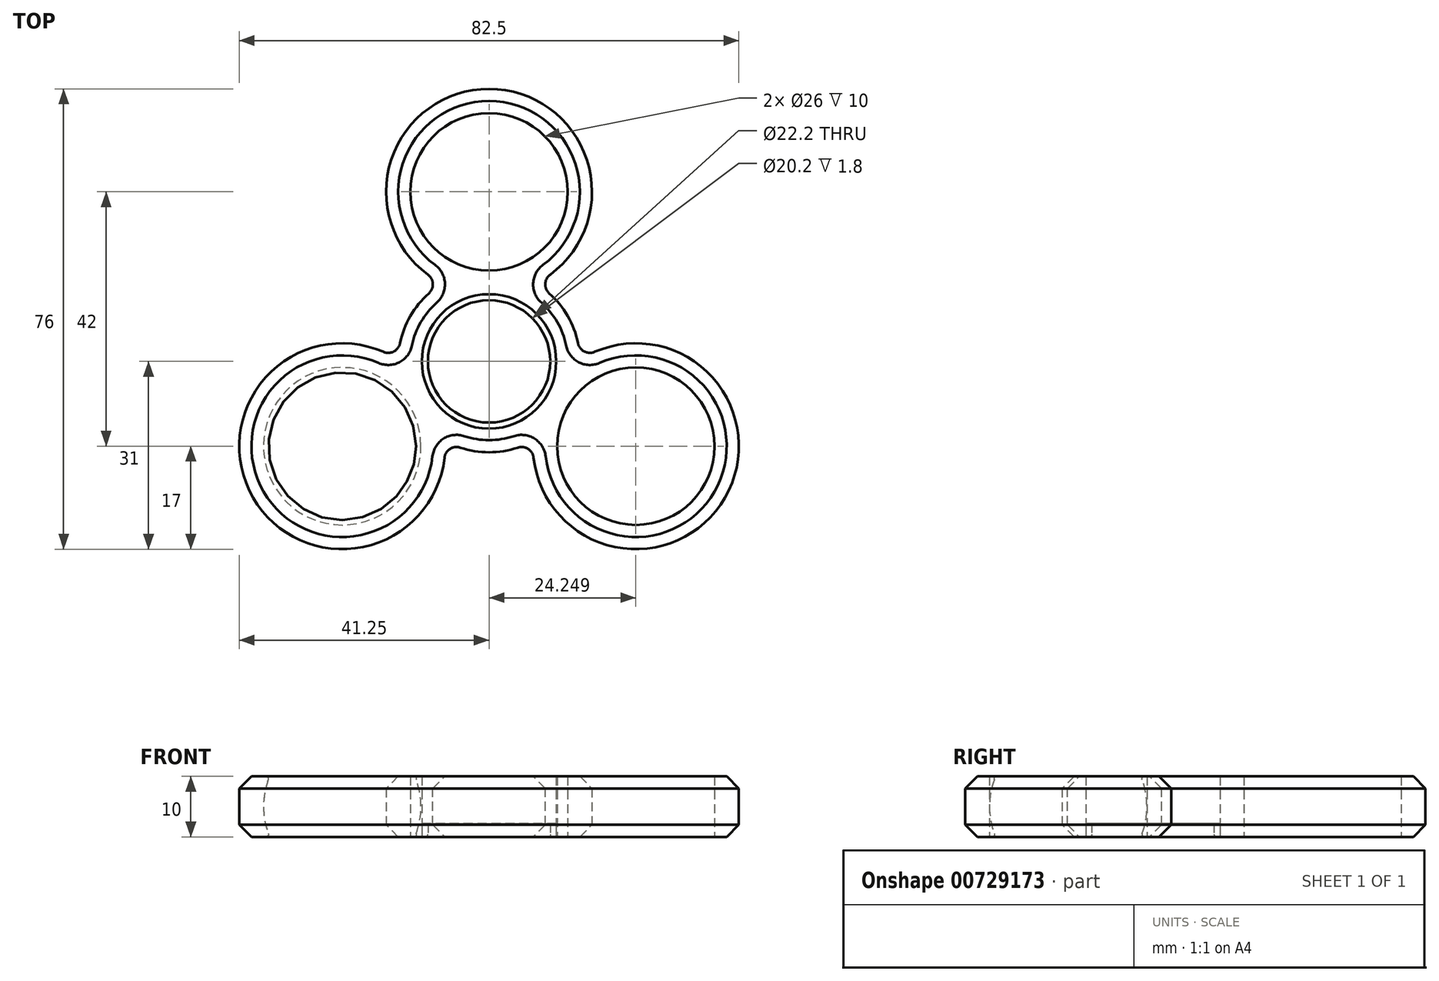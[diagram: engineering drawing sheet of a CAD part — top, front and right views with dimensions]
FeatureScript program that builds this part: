
annotation { "Feature Type Name" : "Feature", "Feature Type Description" : "" }
export const myFeature = defineFeature(function(context is Context, id is Id, definition is map)
    precondition{}
    {
        {
            var Q0;
            Q0=qCreatedBy(makeId("Top.planeOp"),FACE);
            var sketch = newSketch(context, id + "F0", { "sketchPlane" : qUnion([Q0])});
            skLineSegment(sketch, "E0", {"start": v(0, 0) * mm, "end": v(0, 28) * mm, "construction": true});
            skCircle(sketch, "E1", {"center": v(0, 28) * mm, "radius": 13 * mm});
            skArc(sketch, "E2", {"start": v(7.73, 12.86) * mm, "mid": v(0, 45) * mm, "end": v(-7.73, 12.86) * mm});
            skCircle(sketch, "E3", {"center": v(0, 0) * mm, "radius": 11.1 * mm});
            skArc(sketch, "E4", {"start": v(-7.27, -13.12) * mm, "mid": v(0, -15) * mm, "end": v(7.27, -13.12) * mm});
            skArc(sketch, "E5.1.2", {"start": v(-15, 0.26) * mm, "mid": v(-38.97, -22.5) * mm, "end": v(-7.27, -13.12) * mm});
            skCircle(sketch, "E5.1.3", {"center": v(-24.25, -14) * mm, "radius": 13 * mm});
            skArc(sketch, "E5.2.2", {"start": v(7.27, -13.12) * mm, "mid": v(38.97, -22.5) * mm, "end": v(15, 0.26) * mm});
            skCircle(sketch, "E5.2.3", {"center": v(24.25, -14) * mm, "radius": 13 * mm});
            skArc(sketch, "E6.trimOffspring", {"start": v(15, 0.26) * mm, "mid": v(13, 7.5) * mm, "end": v(7.73, 12.86) * mm});
            skArc(sketch, "E7.trimOffspring", {"start": v(-7.73, 12.86) * mm, "mid": v(-13, 7.5) * mm, "end": v(-15, 0.26) * mm});
            skLineSegment(sketch, "E8", {"start": v(0, 0) * mm, "end": v(-24.25, -14) * mm, "construction": true});
            skLineSegment(sketch, "E9", {"start": v(0, 0) * mm, "end": v(24.25, -14) * mm, "construction": true});
            skSolve(sketch);
        }
        {
            var Q0;
            Q0=qSketchRegion(id+"F0",true);
            extrude(context, id + "F1", {"entities" : qUnion([Q0]), "depth" : 10 * mm, "offsetDistance" : 25 * mm});
        }
        {
            var Q0;
            Q0=makeQuery(id+"F1.opExtrude","SWEPT_EDGE",EDGE,{"disambiguationData":[OSD([sQuery(id+"F0.wireOp",EDGE,"E4"),sQuery(id+"F0.wireOp",EDGE,"E5.1.2")])]});
            var Q1;
            Q1=makeQuery(id+"F1.opExtrude","SWEPT_EDGE",EDGE,{"disambiguationData":[OSD([sQuery(id+"F0.wireOp",EDGE,"E4"),sQuery(id+"F0.wireOp",EDGE,"E5.2.2")])]});
            var Q2;
            Q2=makeQuery(id+"F1.opExtrude","SWEPT_EDGE",EDGE,{"disambiguationData":[OSD([sQuery(id+"F0.wireOp",EDGE,"E5.2.2"),sQuery(id+"F0.wireOp",EDGE,"E6.trimOffspring")])]});
            var Q3;
            Q3=makeQuery(id+"F1.opExtrude","SWEPT_EDGE",EDGE,{"disambiguationData":[OSD([sQuery(id+"F0.wireOp",EDGE,"E2"),sQuery(id+"F0.wireOp",EDGE,"E6.trimOffspring")])]});
            var Q4;
            Q4=makeQuery(id+"F1.opExtrude","SWEPT_EDGE",EDGE,{"disambiguationData":[OSD([sQuery(id+"F0.wireOp",EDGE,"E2"),sQuery(id+"F0.wireOp",EDGE,"E7.trimOffspring")])]});
            var Q5;
            Q5=makeQuery(id+"F1.opExtrude","SWEPT_EDGE",EDGE,{"disambiguationData":[OSD([sQuery(id+"F0.wireOp",EDGE,"E5.1.2"),sQuery(id+"F0.wireOp",EDGE,"E7.trimOffspring")])]});
            fillet(context, id + "F2", {"entities" : qUnion([Q0, Q1, Q2, Q3, Q4, Q5]), "radius" : 2 * mm, "tangentPropagation" : true, "allowEdgeOverflow" : false});
        }
        {
            var Q0;
            Q0=makeQuery(id+"F1.opExtrude","CAP_EDGE",EDGE,{"disambiguationData":[OSD([sQuery(id+"F0.wireOp",EDGE,"E5.2.2")])],"isStart":true});
            var Q1;
            Q1=makeQuery(id+"F1.opExtrude","CAP_EDGE",EDGE,{"disambiguationData":[OSD([sQuery(id+"F0.wireOp",EDGE,"E5.2.2")])],"isStart":false});
            chamfer(context, id + "F3", {"entities" : qUnion([Q0, Q1]), "width" : 2 * mm, "tangentPropagation" : true});
        }
        {
            var Q0;
            Q0=qCreatedBy(makeId("Top.planeOp"),FACE);
            var sketch = newSketch(context, id + "F4", { "sketchPlane" : qUnion([Q0])});
            skCircle(sketch, "E10.0", {"center": v(-24.25, -14) * mm, "radius": 13 * mm, "construction": true});
            skLineSegment(sketch, "E11", {"start": v(0, 0) * mm, "end": v(-24.25, -14) * mm, "construction": true});
            skCircle(sketch, "E12.0", {"center": v(0, 28) * mm, "radius": 13 * mm, "construction": true});
            skLineSegment(sketch, "E13", {"start": v(0, 0) * mm, "end": v(0, 28) * mm, "construction": true});
            skCircle(sketch, "E14.0", {"center": v(24.25, -14) * mm, "radius": 13 * mm, "construction": true});
            skLineSegment(sketch, "E15", {"start": v(0, 0) * mm, "end": v(24.25, -14) * mm, "construction": true});
            skSolve(sketch);
        }
        {
            var Q0;
            {var subQ0=sQuery(id+"F0.wireOp",EDGE,"E5.1.2");Q0=makeQuery(id+"F3.opChamfer","BLEND_EDGE",EDGE,{"blendedFrom":[makeQuery(id+"F1.opExtrude","CAP_EDGE",EDGE,{"disambiguationData":[OSD([subQ0])],"isStart":false}),makeQuery(id+"F1.opExtrude","CAP_FACE",FACE,{"disambiguationData":[OSD([sQuery(id+"F0.wireOp",EDGE,"E1"),sQuery(id+"F0.wireOp",EDGE,"E2"),sQuery(id+"F0.wireOp",EDGE,"E3"),sQuery(id+"F0.wireOp",EDGE,"E4"),subQ0,sQuery(id+"F0.wireOp",EDGE,"E5.1.3"),sQuery(id+"F0.wireOp",EDGE,"E5.2.2"),sQuery(id+"F0.wireOp",EDGE,"E5.2.3"),sQuery(id+"F0.wireOp",EDGE,"E6.trimOffspring"),sQuery(id+"F0.wireOp",EDGE,"E7.trimOffspring")])],"isStart":false})],"blendedInto":[makeQuery(id+"F1.opExtrude","CAP_FACE",FACE,{"disambiguationData":[OSD([sQuery(id+"F0.wireOp",EDGE,"E1"),sQuery(id+"F0.wireOp",EDGE,"E2"),sQuery(id+"F0.wireOp",EDGE,"E3"),sQuery(id+"F0.wireOp",EDGE,"E4"),subQ0,sQuery(id+"F0.wireOp",EDGE,"E5.1.3"),sQuery(id+"F0.wireOp",EDGE,"E5.2.2"),sQuery(id+"F0.wireOp",EDGE,"E5.2.3"),sQuery(id+"F0.wireOp",EDGE,"E6.trimOffspring"),sQuery(id+"F0.wireOp",EDGE,"E7.trimOffspring")])],"isStart":false})]});}
            cPoint(context, id + "F5", {"entities" : qUnion([Q0]), "parameter" : 0.5});
        }
        {
            var Q0;
            Q0=sQuery(id+"F4.wireOp",VERTEX,"E11.start");
            var Q1;
            Q1=sQuery(id+"F4.wireOp",VERTEX,"E10.0.center");
            var Q2;
            Q2=qCreatedBy(id+"F5",VERTEX);
            cPlane(context, id + "F6", {"entities" : qUnion([Q0, Q1, Q2]), "cplaneType" : CPlaneType.THREE_POINT, "offset" : 25 * mm, "width" : 150 * mm, "height" : 150 * mm});
        }
        {
            var Q0;
            Q0=qCreatedBy(id+"F6.planeOp",FACE);
            var sketch = newSketch(context, id + "F7", { "sketchPlane" : qUnion([Q0])});
            skLineSegment(sketch, "E16.0", {"start": v(-41, 10) * mm, "end": v(-40, 10) * mm, "construction": true});
            skLineSegment(sketch, "E17.1", {"start": v(-41, 0) * mm, "end": v(-40, 0) * mm, "construction": true});
            skLineSegment(sketch, "E18", {"start": v(-41, 10) * mm, "end": v(-41, 0) * mm});
            skLineSegment(sketch, "E19", {"start": v(-28, 0) * mm, "end": v(-28, 10) * mm, "construction": true});
            skArc(sketch, "E20", {"start": v(-40, 10) * mm, "mid": v(-41, 5) * mm, "end": v(-40, 0) * mm});
            skLineSegment(sketch, "E21", {"start": v(-41, 10) * mm, "end": v(-40, 10) * mm});
            skLineSegment(sketch, "E22", {"start": v(-41, 0) * mm, "end": v(-40, 0) * mm});
            skLineSegment(sketch, "E23.trimOffspring", {"start": v(-28, 10) * mm, "end": v(-15, 10) * mm, "construction": true});
            skLineSegment(sketch, "E24.trimOffspring", {"start": v(-28, 0) * mm, "end": v(-15, 0) * mm, "construction": true});
            skSolve(sketch);
        }
        {
            var Q0;
            Q0=qSketchRegion(id+"F7",true);
            var Q1;
            Q1=sQuery(id+"F7.wireOp",EDGE,"E19");
            revolve(context, id + "F8", {"operationType" : NewBodyOperationType.ADD, "surfaceOperationType" : NewSurfaceOperationType.NEW, "entities" : qUnion([Q0]), "axis" : qUnion([Q1]), "revolveType" : RevolveType.FULL});
        }
        {
            var Q0;
            {var subQ0=sQuery(id+"F7.wireOp",EDGE,"E22");Q0=makeQuery(id+"FEcUt43eDZ80vxZ_1.2.F8.boolean.opBoolean","MERGE",FACE,{"derivedFrom":[makeQuery(id+"Fynh9oEJvHPlE7w_1.2.F8.boolean.opBoolean","MERGE",FACE,{"derivedFrom":[makeQuery(id+"F8.boolean.opBoolean","MERGE",FACE,{"derivedFrom":[makeQuery(id+"F1.opExtrude","CAP_FACE",FACE,{"disambiguationData":[OSD([sQuery(id+"F0.wireOp",EDGE,"E1"),sQuery(id+"F0.wireOp",EDGE,"E2"),sQuery(id+"F0.wireOp",EDGE,"E3"),sQuery(id+"F0.wireOp",EDGE,"E4"),sQuery(id+"F0.wireOp",EDGE,"E5.1.2"),sQuery(id+"F0.wireOp",EDGE,"E5.1.3"),sQuery(id+"F0.wireOp",EDGE,"E5.2.2"),sQuery(id+"F0.wireOp",EDGE,"E5.2.3"),sQuery(id+"F0.wireOp",EDGE,"E6.trimOffspring"),sQuery(id+"F0.wireOp",EDGE,"E7.trimOffspring")])],"isStart":true}),makeQuery(id+"F8.opRevolve","SWEPT_FACE",FACE,{"disambiguationData":[OSD([subQ0])]})]}),makeQuery(id+"Fynh9oEJvHPlE7w_1.2.F8.opRevolve","SWEPT_FACE",FACE,{"disambiguationData":[OSD([subQ0])]})]}),makeQuery(id+"FEcUt43eDZ80vxZ_1.2.F8.opRevolve","SWEPT_FACE",FACE,{"disambiguationData":[OSD([subQ0])]})]});}
            var sketch = newSketch(context, id + "F9", { "sketchPlane" : qUnion([Q0])});
            skCircle(sketch, "E25", {"center": v(0, 0) * mm, "radius": 10.1 * mm});
            skCircle(sketch, "E26.0", {"center": v(0, 0) * mm, "radius": 11.1 * mm});
            skSolve(sketch);
        }
        {
            var Q0;
            Q0 = qSketchRegion(id + "F9", true);
            extrude(context, id + "F10", {"entities" : qUnion([Q0]), "oppositeDirection" : true, "depth" : 2.2 * mm, "offsetDistance" : 25 * mm});
        }
        {
            var Q0;
            Q0=makeQuery(id+"F8.opRevolve","SWEPT_EDGE",EDGE,{"disambiguationData":[OSD([sQuery(id+"F7.wireOp",EDGE,"E20"),sQuery(id+"F7.wireOp",EDGE,"E21")])]});
            var Q1;
            Q1=makeQuery(id+"F8.opRevolve","SWEPT_EDGE",EDGE,{"disambiguationData":[OSD([sQuery(id+"F7.wireOp",EDGE,"E20"),sQuery(id+"F7.wireOp",EDGE,"E22")])]});
            var Q2;
            Q2=makeQuery(id+"FEcUt43eDZ80vxZ_1.2.F8.opRevolve","SWEPT_EDGE",EDGE,{"disambiguationData":[OSD([sQuery(id+"F7.wireOp",EDGE,"E20"),sQuery(id+"F7.wireOp",EDGE,"E21")])]});
            var Q3;
            Q3=makeQuery(id+"FEcUt43eDZ80vxZ_1.2.F8.opRevolve","SWEPT_EDGE",EDGE,{"disambiguationData":[OSD([sQuery(id+"F7.wireOp",EDGE,"E20"),sQuery(id+"F7.wireOp",EDGE,"E22")])]});
            var Q4;
            Q4=makeQuery(id+"Fynh9oEJvHPlE7w_1.2.F8.opRevolve","SWEPT_EDGE",EDGE,{"disambiguationData":[OSD([sQuery(id+"F7.wireOp",EDGE,"E20"),sQuery(id+"F7.wireOp",EDGE,"E21")])]});
            var Q5;
            Q5=makeQuery(id+"Fynh9oEJvHPlE7w_1.2.F8.opRevolve","SWEPT_EDGE",EDGE,{"disambiguationData":[OSD([sQuery(id+"F7.wireOp",EDGE,"E20"),sQuery(id+"F7.wireOp",EDGE,"E22")])]});
            var Q6;
            Q6=makeQuery(id+"F10.opExtrude","CAP_EDGE",EDGE,{"disambiguationData":[OSD([sQuery(id+"F9.wireOp",EDGE,"E25")])],"isStart":true});
            fillet(context, id + "F11", {"entities" : qUnion([Q0, Q1, Q2, Q3, Q4, Q5, Q6]), "radius" : .4 * mm, "tangentPropagation" : true, "allowEdgeOverflow" : false});
        }
    });
